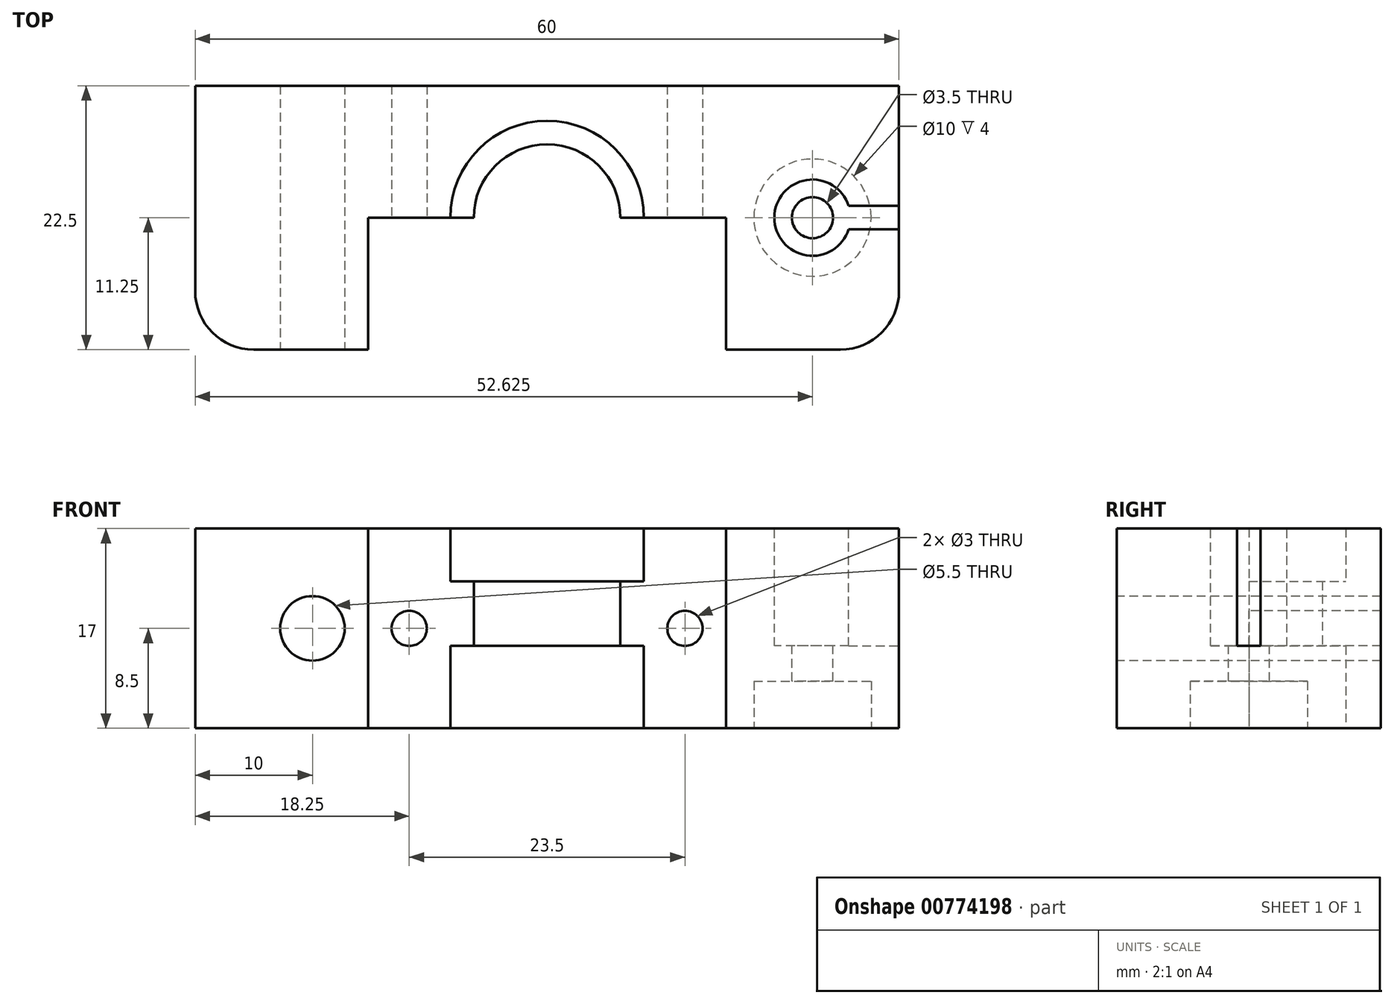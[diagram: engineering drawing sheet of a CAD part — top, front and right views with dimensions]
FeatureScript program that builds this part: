
annotation { "Feature Type Name" : "Feature", "Feature Type Description" : "" }
export const myFeature = defineFeature(function(context is Context, id is Id, definition is map)
    precondition{}
    {
        {
            var Q0;
            Q0=qCreatedBy(makeId("Top.planeOp"),FACE);
            var sketch = newSketch(context, id + "F0", { "sketchPlane" : qUnion([Q0])});
            skArc(sketch, "E0", {"start": v(8.25, 0) * mm, "mid": v(0, 8.25) * mm, "end": v(-8.25, 0) * mm});
            skLineSegment(sketch, "E1", {"start": v(0, 11.25) * mm, "end": v(-30, 11.25) * mm});
            skLineSegment(sketch, "E2", {"start": v(-30, -11.25) * mm, "end": v(-15.25, -11.25) * mm});
            skLineSegment(sketch, "E3", {"start": v(-15.25, -11.25) * mm, "end": v(-15.25, 0) * mm});
            skLineSegment(sketch, "E4", {"start": v(-15.25, 0) * mm, "end": v(-8.25, 0) * mm});
            skLineSegment(sketch, "E5.MirrorCS", {"start": v(0, 11.25) * mm, "end": v(30, 11.25) * mm});
            skLineSegment(sketch, "E6.MirrorCS", {"start": v(30, 11.25) * mm, "end": v(30, -11.25) * mm});
            skLineSegment(sketch, "E7.MirrorCS", {"start": v(30, -11.25) * mm, "end": v(15.25, -11.25) * mm});
            skLineSegment(sketch, "E8.MirrorCS", {"start": v(15.25, -11.25) * mm, "end": v(15.25, 0) * mm});
            skLineSegment(sketch, "E9.MirrorCS", {"start": v(15.25, 0) * mm, "end": v(8.25, 0) * mm});
            skLineSegment(sketch, "E10", {"start": v(-30, 11.25) * mm, "end": v(-30, 0) * mm});
            skLineSegment(sketch, "E11", {"start": v(-30, 0) * mm, "end": v(-30, -11.25) * mm});
            skSolve(sketch);
        }
        {
            var Q0;
            Q0 = qSketchRegion(id + "F0", true);
            extrude(context, id + "F1", {"entities" : qUnion([Q0]), "depth" : 17 * mm, "offsetDistance" : 25 * mm, "symmetric" : true});
        }
        {
            var Q0;
            Q0=makeQuery(id+"F1.opExtrude","SWEPT_FACE",FACE,{"disambiguationData":[OSD([sQuery(id+"F0.wireOp",EDGE,"E2")])]});
            var sketch = newSketch(context, id + "F2", { "sketchPlane" : qUnion([Q0])});
            skCircle(sketch, "E12", {"center": v(-20, 0) * mm, "radius": 2.75 * mm});
            skSolve(sketch);
        }
        {
            var Q0;
            Q0 = qSketchRegion(id + "F2", true);
            extrude(context, id + "F3", {"entities" : qUnion([Q0]), "operationType" : NewBodyOperationType.REMOVE, "endBound" : BoundingType.THROUGH_ALL, "oppositeDirection" : true, "depth" : 25 * mm, "offsetDistance" : 25 * mm});
        }
        {
            var Q0;
            Q0=makeQuery(id+"F1.opExtrude","CAP_FACE",FACE,{"disambiguationData":[OSD([sQuery(id+"F0.wireOp",EDGE,"E0"),sQuery(id+"F0.wireOp",EDGE,"E1"),sQuery(id+"F0.wireOp",EDGE,"E2"),sQuery(id+"F0.wireOp",EDGE,"E3"),sQuery(id+"F0.wireOp",EDGE,"E4"),sQuery(id+"F0.wireOp",EDGE,"E5.MirrorCS"),sQuery(id+"F0.wireOp",EDGE,"E6.MirrorCS"),sQuery(id+"F0.wireOp",EDGE,"E7.MirrorCS"),sQuery(id+"F0.wireOp",EDGE,"E8.MirrorCS"),sQuery(id+"F0.wireOp",EDGE,"E9.MirrorCS"),sQuery(id+"F0.wireOp",EDGE,"E10"),sQuery(id+"F0.wireOp",EDGE,"E11")])],"isStart":false});
            var sketch = newSketch(context, id + "F4", { "sketchPlane" : qUnion([Q0])});
            skCircle(sketch, "E13", {"center": v(22.62, 0) * mm, "radius": 1.75 * mm});
            skPoint(sketch, "E13.centerSnap0", {"position": v(22.62, -11.25) * mm});
            skSolve(sketch);
        }
        {
            var Q0;
            Q0 = qSketchRegion(id + "F4", true);
            extrude(context, id + "F5", {"entities" : qUnion([Q0]), "operationType" : NewBodyOperationType.REMOVE, "endBound" : BoundingType.THROUGH_ALL, "oppositeDirection" : true, "depth" : 25 * mm, "offsetDistance" : 25 * mm});
        }
        {
            var Q0;
            Q0=makeQuery(id+"F1.opExtrude","CAP_FACE",FACE,{"disambiguationData":[OSD([sQuery(id+"F0.wireOp",EDGE,"E0"),sQuery(id+"F0.wireOp",EDGE,"E1"),sQuery(id+"F0.wireOp",EDGE,"E2"),sQuery(id+"F0.wireOp",EDGE,"E3"),sQuery(id+"F0.wireOp",EDGE,"E4"),sQuery(id+"F0.wireOp",EDGE,"E5.MirrorCS"),sQuery(id+"F0.wireOp",EDGE,"E6.MirrorCS"),sQuery(id+"F0.wireOp",EDGE,"E7.MirrorCS"),sQuery(id+"F0.wireOp",EDGE,"E8.MirrorCS"),sQuery(id+"F0.wireOp",EDGE,"E9.MirrorCS"),sQuery(id+"F0.wireOp",EDGE,"E10"),sQuery(id+"F0.wireOp",EDGE,"E11")])],"isStart":true});
            var sketch = newSketch(context, id + "F6", { "sketchPlane" : qUnion([Q0])});
            skCircle(sketch, "E14", {"center": v(22.62, 0) * mm, "radius": 5 * mm});
            skSolve(sketch);
        }
        {
            var Q0;
            Q0 = qSketchRegion(id + "F6", true);
            extrude(context, id + "F7", {"entities" : qUnion([Q0]), "operationType" : NewBodyOperationType.REMOVE, "oppositeDirection" : true, "depth" : 4 * mm, "offsetDistance" : 25 * mm});
        }
        {
            var Q0;
            Q0=makeQuery(id+"F1.opExtrude","SWEPT_FACE",FACE,{"disambiguationData":[OSD([sQuery(id+"F0.wireOp",EDGE,"E4")])]});
            var sketch = newSketch(context, id + "F8", { "sketchPlane" : qUnion([Q0])});
            skLineSegment(sketch, "E15", {"start": v(-11.75, -8.5) * mm, "end": v(-11.75, 8.5) * mm, "construction": true});
            skCircle(sketch, "E16", {"center": v(-11.75, 0) * mm, "radius": 1.5 * mm});
            skCircle(sketch, "E17.MirrorC", {"center": v(11.75, 0) * mm, "radius": 1.5 * mm});
            skSolve(sketch);
        }
        {
            var Q0;
            Q0 = qSketchRegion(id + "F8", true);
            extrude(context, id + "F9", {"entities" : qUnion([Q0]), "operationType" : NewBodyOperationType.REMOVE, "endBound" : BoundingType.THROUGH_ALL, "oppositeDirection" : true, "depth" : 25 * mm, "offsetDistance" : 25 * mm});
        }
        {
            var Q0;
            Q0=makeQuery(id+"F1.opExtrude","SWEPT_EDGE",EDGE,{"disambiguationData":[OSD([sQuery(id+"F0.wireOp",EDGE,"E2"),sQuery(id+"F0.wireOp",EDGE,"E11")])]});
            var Q1;
            Q1=makeQuery(id+"F1.opExtrude","SWEPT_EDGE",EDGE,{"disambiguationData":[OSD([sQuery(id+"F0.wireOp",EDGE,"E6.MirrorCS"),sQuery(id+"F0.wireOp",EDGE,"E7.MirrorCS")])]});
            fillet(context, id + "F10", {"entities" : qUnion([Q0, Q1]), "radius" : 5 * mm, "tangentPropagation" : true, "allowEdgeOverflow" : false});
        }
        {
            var Q0;
            Q0=makeQuery(id+"F1.opExtrude","CAP_FACE",FACE,{"disambiguationData":[OSD([sQuery(id+"F0.wireOp",EDGE,"E0"),sQuery(id+"F0.wireOp",EDGE,"E1"),sQuery(id+"F0.wireOp",EDGE,"E2"),sQuery(id+"F0.wireOp",EDGE,"E3"),sQuery(id+"F0.wireOp",EDGE,"E4"),sQuery(id+"F0.wireOp",EDGE,"E5.MirrorCS"),sQuery(id+"F0.wireOp",EDGE,"E6.MirrorCS"),sQuery(id+"F0.wireOp",EDGE,"E7.MirrorCS"),sQuery(id+"F0.wireOp",EDGE,"E8.MirrorCS"),sQuery(id+"F0.wireOp",EDGE,"E9.MirrorCS"),sQuery(id+"F0.wireOp",EDGE,"E10"),sQuery(id+"F0.wireOp",EDGE,"E11")])],"isStart":false});
            var sketch = newSketch(context, id + "F11", { "sketchPlane" : qUnion([Q0])});
            skArc(sketch, "E18", {"start": v(25.72, 1) * mm, "mid": v(19.38, 0) * mm, "end": v(25.72, -1) * mm});
            skLineSegment(sketch, "E19", {"start": v(25.72, 1) * mm, "end": v(30, 1) * mm});
            skLineSegment(sketch, "E20", {"start": v(30, 1) * mm, "end": v(30, 0) * mm});
            skLineSegment(sketch, "E21.MirrorCS", {"start": v(25.72, -1) * mm, "end": v(30, -1) * mm});
            skLineSegment(sketch, "E22.MirrorCS", {"start": v(30, -1) * mm, "end": v(30, 0) * mm});
            skSolve(sketch);
        }
        {
            var Q0;
            Q0 = qSketchRegion(id + "F11", true);
            extrude(context, id + "F12", {"entities" : qUnion([Q0]), "operationType" : NewBodyOperationType.REMOVE, "oppositeDirection" : true, "depth" : 10 * mm, "offsetDistance" : 25 * mm});
        }
        {
            var Q0;
            Q0=qCreatedBy(makeId("Top.planeOp"),FACE);
            cPlane(context, id + "F13", {"entities" : qUnion([Q0]), "cplaneType" : CPlaneType.OFFSET, "offset" : 1.25 * mm, "width" : 150 * mm, "height" : 150 * mm});
        }
        {
            var Q0;
            Q0=qCreatedBy(id+"F13.planeOp",FACE);
            var sketch = newSketch(context, id + "F14", { "sketchPlane" : qUnion([Q0])});
            skArc(sketch, "E23", {"start": v(9, 0) * mm, "mid": v(0, 9) * mm, "end": v(-9, 0) * mm});
            skArc(sketch, "E24", {"start": v(6.25, 0) * mm, "mid": v(0, 6.25) * mm, "end": v(-6.25, 0) * mm});
            skLineSegment(sketch, "E25", {"start": v(-9, 0) * mm, "end": v(-6.25, 0) * mm});
            skLineSegment(sketch, "E26", {"start": v(6.25, 0) * mm, "end": v(9, 0) * mm});
            skSolve(sketch);
        }
        {
            var Q0;
            Q0 = qSketchRegion(id + "F14", true);
            extrude(context, id + "F15", {"entities" : qUnion([Q0]), "operationType" : NewBodyOperationType.ADD, "depth" : 5.5 * mm, "offsetDistance" : 25 * mm, "symmetric" : true});
        }
    });
